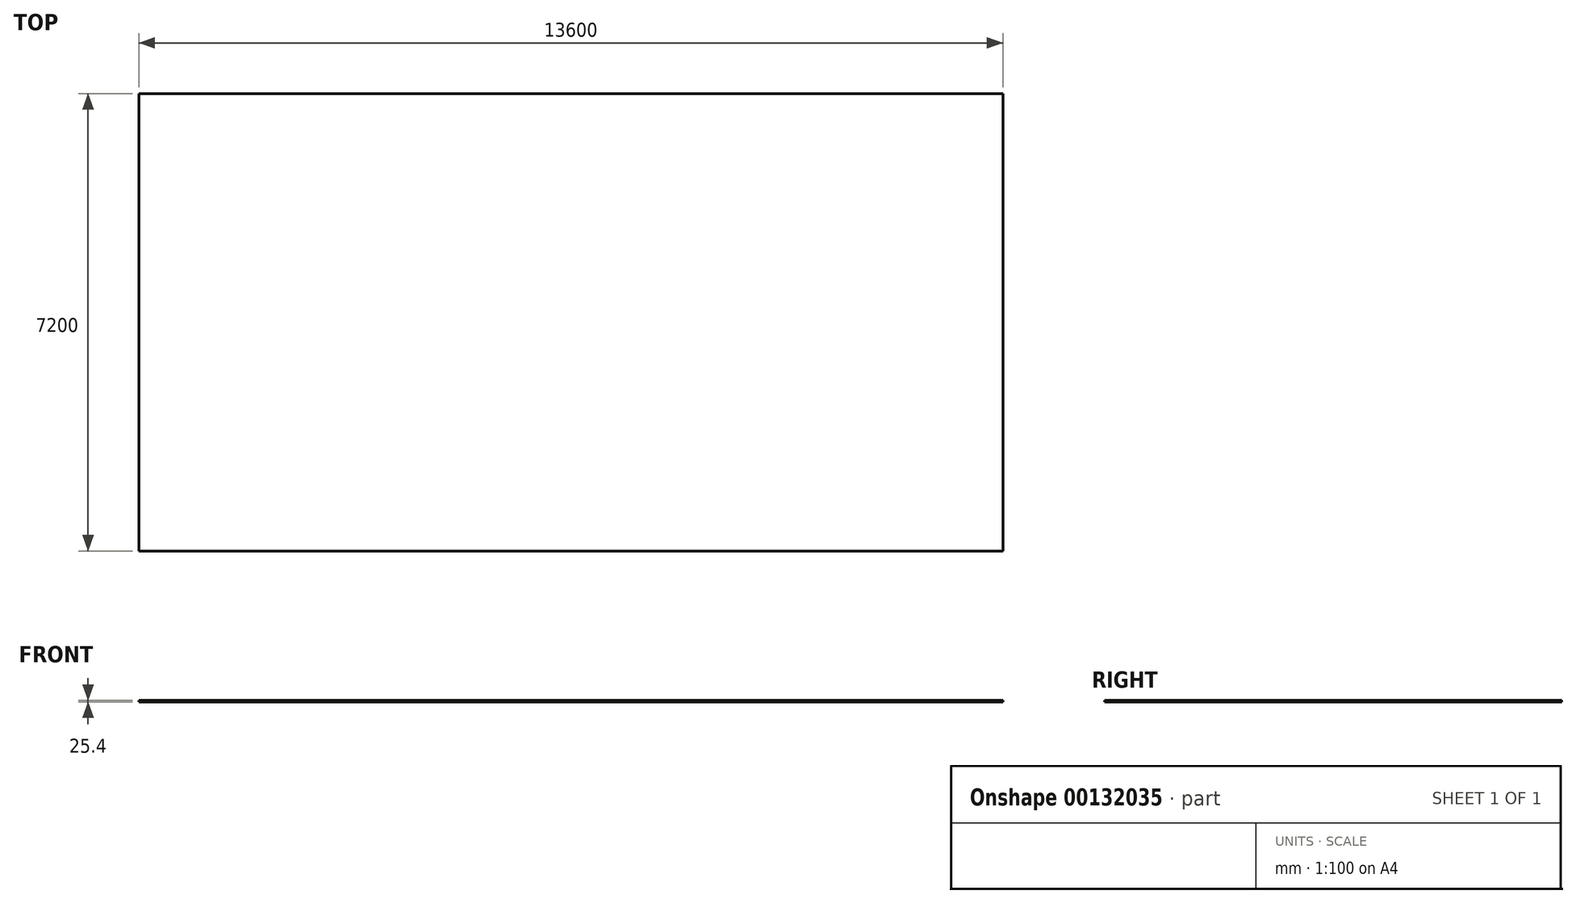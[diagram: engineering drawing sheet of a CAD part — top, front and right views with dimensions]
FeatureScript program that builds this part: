
annotation { "Feature Type Name" : "Feature", "Feature Type Description" : "" }
export const myFeature = defineFeature(function(context is Context, id is Id, definition is map)
    precondition{}
    {
        {
            var Q0;
            Q0=qCreatedBy(makeId("Top.planeOp"),FACE);
            var sketch = newSketch(context, id + "F0", { "sketchPlane" : qUnion([Q0])});
            skLineSegment(sketch, "E0.bottom", {"start": v(-6800, -3600) * mm, "end": v(6800, -3600) * mm});
            skLineSegment(sketch, "E0.top", {"start": v(-6800, 3600) * mm, "end": v(6800, 3600) * mm});
            skLineSegment(sketch, "E0.left", {"start": v(-6800, -3600) * mm, "end": v(-6800, 3600) * mm});
            skLineSegment(sketch, "E0.right", {"start": v(6800, -3600) * mm, "end": v(6800, 3600) * mm});
            skPoint(sketch, "E0.middle", {"position": v(0, 0) * mm});
            skSolve(sketch);
        }
        {
            var Q0;
            Q0 = qSketchRegion(id + "F0", true);
            extrude(context, id + "F1", {"entities" : qUnion([Q0]), "depth" : 25.4 * mm});
        }
    });
